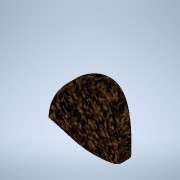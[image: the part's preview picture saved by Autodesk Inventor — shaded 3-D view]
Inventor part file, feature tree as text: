
AUTODESK INVENTOR PART (.ipt)
format: ipt  version: 2021 (Build 250183000, 183)  size: 229,376 bytes
history: native  units: mm
features: extrude x1, fillet x1, sketch x1
ambient origin geometry x8: Origin, YZ Plane, XZ Plane, XY Plane, X Axis, Y Axis, Z Axis, Center Point
bodies: Solid1 (feature_tree)
feature tree (3):
  extrude  "Extrusion1"  Depth=2.0mm
  fillet  "Fillet2"  Radius=0.5mm
  sketch  "Sketch1"  dims[d0=10.0mm d1=0.0mm d3=2.0mm d2=0.5mm]
